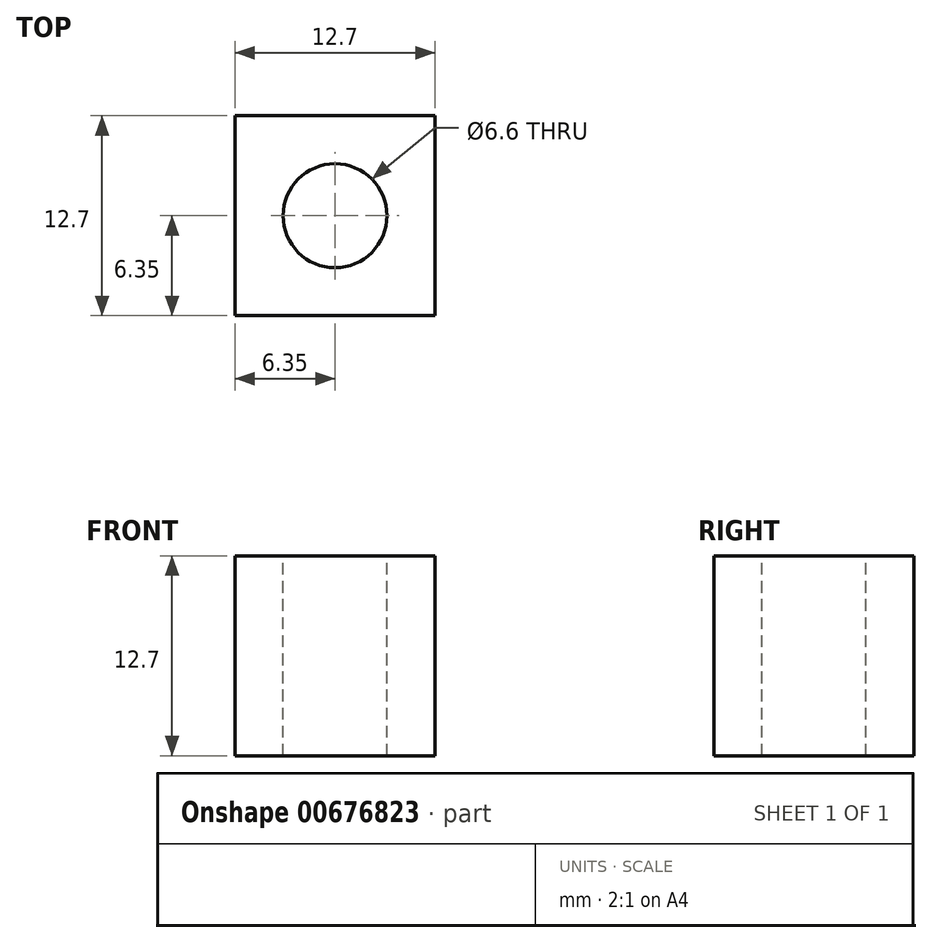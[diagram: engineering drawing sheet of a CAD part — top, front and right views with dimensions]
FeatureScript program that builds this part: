
annotation { "Feature Type Name" : "Feature", "Feature Type Description" : "" }
export const myFeature = defineFeature(function(context is Context, id is Id, definition is map)
    precondition{}
    {
        {
            var Q0;
            Q0=qCreatedBy(makeId("Top.planeOp"),FACE);
            var sketch = newSketch(context, id + "F0", { "sketchPlane" : qUnion([Q0])});
            skLineSegment(sketch, "E0.bottom", {"start": v(6.35, -6.35) * mm, "end": v(-6.35, -6.35) * mm});
            skLineSegment(sketch, "E0.top", {"start": v(6.35, 6.35) * mm, "end": v(-6.35, 6.35) * mm});
            skLineSegment(sketch, "E0.left", {"start": v(6.35, -6.35) * mm, "end": v(6.35, 6.35) * mm});
            skLineSegment(sketch, "E0.right", {"start": v(-6.35, -6.35) * mm, "end": v(-6.35, 6.35) * mm});
            skPoint(sketch, "E0.middle", {"position": v(0, 0) * mm});
            skCircle(sketch, "E1", {"center": v(0, 0) * mm, "radius": 3.3 * mm});
            skSolve(sketch);
        }
        {
            var Q0;
            Q0=makeQuery(id+"F0.imprint","IMPRINT",FACE,{"disambiguationData":[TD([[makeQuery(id+"F0.imprint","IMPRINT",EDGE,{"derivedFrom":sQuery(id+"F0.wireOp",EDGE,"E0.bottom")}),-1.0]])]});
            extrude(context, id + "F1", {"entities" : qUnion([Q0]), "oppositeDirection" : true, "depth" : 12.7 * mm, "offsetDistance" : 25.4 * mm});
        }
    });
